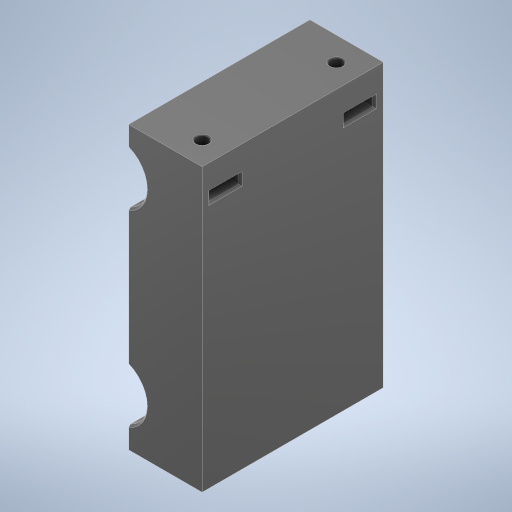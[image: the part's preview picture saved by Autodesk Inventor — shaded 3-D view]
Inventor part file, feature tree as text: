
AUTODESK INVENTOR PART (.ipt)
format: ipt  version: 2023 (Build 270158000, 158)  size: 305,152 bytes
history: native  units: in
note: dims shown in document units (in); Inventor stores cm internally (conversion verified against a paired STEP export)
features: sketch x4, extrude x3, chamfer x2, plane x2, hole x1, fillet x1
ambient origin geometry x8: Origin, YZ Plane, XZ Plane, XY Plane, X Axis, Y Axis, Z Axis, Center Point
bodies: Solid1 (feature_tree)
feature tree (13):
  extrude  "Extrusion1"  Depth=3.0in
  chamfer  "Chamfer1"  Distance=2.0in
  plane  "Work Plane1"
  plane  "Work Plane2"
  extrude  "Extrusion3"  Depth=0.5in
  hole  "Hole1"  [1 undecoded]
  extrude  "Extrusion4"  Depth=1.9291in TaperAngle=0.0deg
  fillet  "Fillet1"  Radius=0.02in
  chamfer  "Chamfer2"  Distance=0.1181in
  sketch  "Sketch1"  dims[d0=3.0in d1=0.5956in]
  sketch  "Sketch4"  dims[d2=0.5956in]
  sketch  "Sketch5"  dims[d3=1.8in]
  sketch  "Sketch6"  dims[d4=0.5in d5=2.0in d7=0.5in d8=0.0in d9=1.9291in d10=0.0in d11=0.02in d12=0.125in d13=45.0deg d25=0.0in d26=0.1181in d27=3.937in d28=0.0in d29=0.2096in d30=0.25in d31=0.25in d32=0.25in d33=0.25in d34=0.1339in d35=0.2953in d36=0.2559in d37=0.1181in d38=90.0deg d39=0.3937in d40=0.8108in d41=0.0984in d42=0.2756in d43=0.315in d44=0.5256in d45=0.0in d46=0.0079in d47=0.0197in d48=0.0492in d49=45.0deg]
note: 1 required parameter value undecoded (feature->parameter linkage not recoverable at this tier; creation-order binding heuristic only, values carry confidence <= 0.55)
